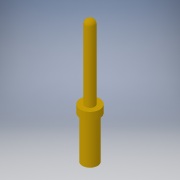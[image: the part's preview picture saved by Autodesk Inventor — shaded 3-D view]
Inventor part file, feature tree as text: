
AUTODESK INVENTOR PART (.ipt)
format: ipt  version: 2019 (Build 230136000, 136)  size: 119,296 bytes
history: native  units: in
note: dims shown in document units (in); Inventor stores cm internally (conversion verified against a paired STEP export)
features: extrude x3, sketch x3, projected_geometry x2, fillet x1
ambient origin geometry x8: Origin, YZ Plane, XZ Plane, XY Plane, X Axis, Y Axis, Z Axis, Center Point
bodies: Solid1 (feature_tree)
feature tree (9):
  extrude  "Extrusion1"  Depth=0.185in TaperAngle=0.0deg
  extrude  "Extrusion2"  Depth=0.033in TaperAngle=0.0deg
  extrude  "Extrusion3"  Depth=0.325in TaperAngle=0.0deg
  fillet  "Fillet1"  Radius=0.02in
  sketch  "Sketch1"  dims[d0=0.067in d1=0.185in d2=0.0in]
  sketch  "Sketch2"  dims[d3=0.085in d4=0.033in d5=0.0in]
  projected_geometry  "Projected Loop1"
  sketch  "Sketch3"  dims[d6=0.041in d7=0.325in d8=0.0in d9=0.02in]
  projected_geometry  "Projected Loop2"
